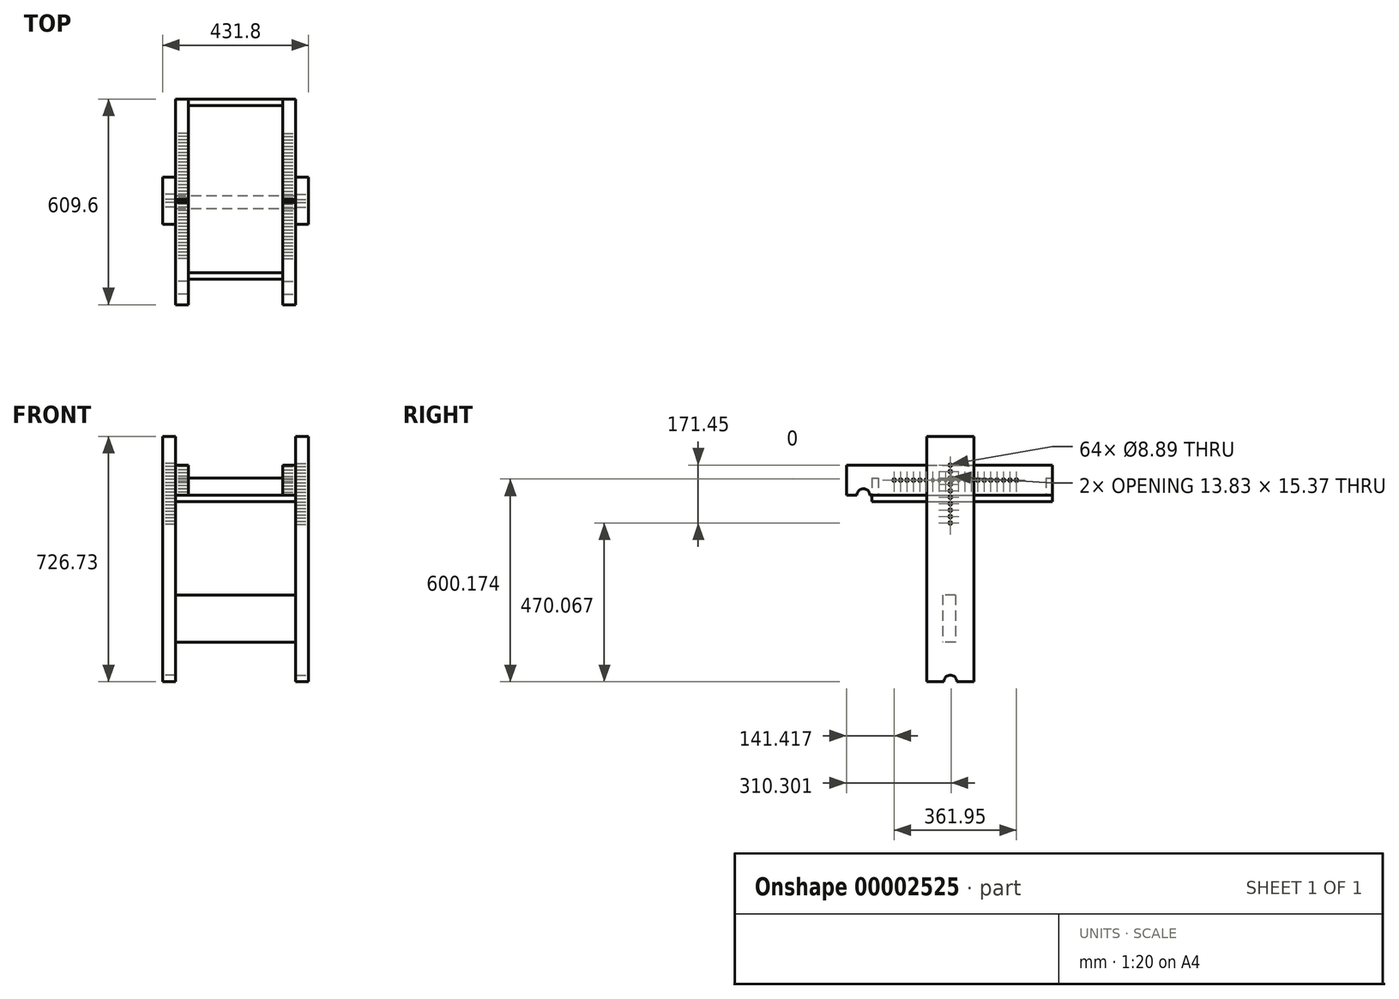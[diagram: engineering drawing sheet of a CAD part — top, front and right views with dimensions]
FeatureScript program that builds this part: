
annotation { "Feature Type Name" : "Feature", "Feature Type Description" : "" }
export const myFeature = defineFeature(function(context is Context, id is Id, definition is map)
    precondition{}
    {
        {
            var Q0;
            Q0=qCreatedBy(makeId("Right.planeOp"),FACE);
            var sketch = newSketch(context, id + "F0", { "sketchPlane" : qUnion([Q0])});
            skLineSegment(sketch, "E0", {"start": v(-273.03, 718.1) * mm, "end": v(285.89, -480.5) * mm, "construction": true});
            skLineSegment(sketch, "E1", {"start": v(-191.78, 754.22) * mm, "end": v(359.92, -428.91) * mm, "construction": true});
            skLineSegment(sketch, "E2", {"start": v(285.89, -480.5) * mm, "end": v(-310.41, -480.5) * mm, "construction": true});
            skLineSegment(sketch, "E3", {"start": v(-170.79, 498.85) * mm, "end": v(-90.22, 536.42) * mm, "construction": true});
            skCircle(sketch, "E4", {"center": v(-130.5, 517.63) * mm, "radius": 19.05 * mm, "construction": true});
            skLineSegment(sketch, "E5", {"start": v(86.84, -53.64) * mm, "end": v(167.41, -16.07) * mm, "construction": true});
            skCircle(sketch, "E6", {"center": v(127.13, -34.85) * mm, "radius": 19.05 * mm, "construction": true});
            skSolve(sketch);
        }
        {
            var Q0;
            Q0=qCreatedBy(makeId("Right.planeOp"),FACE);
            var sketch = newSketch(context, id + "F1", { "sketchPlane" : qUnion([Q0])});
            skLineSegment(sketch, "E7.bottom", {"start": v(-180.61, 606.53) * mm, "end": v(428.99, 606.53) * mm});
            skLineSegment(sketch, "E7.top", {"start": v(-180.61, 517.63) * mm, "end": v(428.99, 517.63) * mm});
            skLineSegment(sketch, "E7.left", {"start": v(-180.61, 606.53) * mm, "end": v(-180.61, 517.63) * mm});
            skLineSegment(sketch, "E7.right", {"start": v(428.99, 606.53) * mm, "end": v(428.99, 517.63) * mm});
            skSolve(sketch);
        }
        {
            var Q0;
            Q0 = qSketchRegion(id + "F1", true);
            extrude(context, id + "F2", {"entities" : qUnion([Q0]), "oppositeDirection" : true, "depth" : 38.1 * mm});
        }
        {
            var Q0;
            Q0=makeQuery(id+"F2.opExtrude","CAP_FACE",FACE,{"disambiguationData":[OSD([sQuery(id+"F1.wireOp",EDGE,"E7.bottom"),sQuery(id+"F1.wireOp",EDGE,"E7.top"),sQuery(id+"F1.wireOp",EDGE,"E7.left"),sQuery(id+"F1.wireOp",EDGE,"E7.right")])],"isStart":true});
            var sketch = newSketch(context, id + "F3", { "sketchPlane" : qUnion([Q0])});
            skLineSegment(sketch, "E8", {"start": v(-180.61, 562.08) * mm, "end": v(428.99, 562.08) * mm, "construction": true});
            skCircle(sketch, "E9", {"center": v(-39.2, 562.08) * mm, "radius": 4.45 * mm});
            skCircle(sketch, "E10.1.0.0", {"center": v(-20.14, 562.08) * mm, "radius": 4.45 * mm});
            skCircle(sketch, "E10.2.0.0", {"center": v(-1.1, 562.08) * mm, "radius": 4.45 * mm});
            skCircle(sketch, "E10.3.0.0", {"center": v(17.96, 562.08) * mm, "radius": 4.45 * mm});
            skCircle(sketch, "E10.4.0.0", {"center": v(37, 562.08) * mm, "radius": 4.45 * mm});
            skCircle(sketch, "E10.5.0.0", {"center": v(56.06, 562.08) * mm, "radius": 4.45 * mm});
            skCircle(sketch, "E10.6.0.0", {"center": v(75.1, 562.08) * mm, "radius": 4.45 * mm});
            skCircle(sketch, "E10.7.0.0", {"center": v(94.16, 562.08) * mm, "radius": 4.45 * mm});
            skCircle(sketch, "E10.8.0.0", {"center": v(113.2, 562.08) * mm, "radius": 4.45 * mm});
            skCircle(sketch, "E10.9.0.0", {"center": v(132.26, 562.08) * mm, "radius": 4.45 * mm});
            skCircle(sketch, "E10.10.0.0", {"center": v(151.3, 562.08) * mm, "radius": 4.45 * mm});
            skCircle(sketch, "E10.11.0.0", {"center": v(170.36, 562.08) * mm, "radius": 4.45 * mm});
            skCircle(sketch, "E10.12.0.0", {"center": v(189.4, 562.08) * mm, "radius": 4.45 * mm});
            skCircle(sketch, "E10.13.0.0", {"center": v(208.46, 562.08) * mm, "radius": 4.45 * mm});
            skCircle(sketch, "E10.14.0.0", {"center": v(227.5, 562.08) * mm, "radius": 4.45 * mm});
            skCircle(sketch, "E10.15.0.0", {"center": v(246.56, 562.08) * mm, "radius": 4.45 * mm});
            skCircle(sketch, "E10.16.0.0", {"center": v(265.6, 562.08) * mm, "radius": 4.45 * mm});
            skCircle(sketch, "E10.17.0.0", {"center": v(284.66, 562.08) * mm, "radius": 4.45 * mm});
            skCircle(sketch, "E10.18.0.0", {"center": v(303.7, 562.08) * mm, "radius": 4.45 * mm});
            skCircle(sketch, "E10.19.0.0", {"center": v(322.76, 562.08) * mm, "radius": 4.45 * mm});
            skLineSegment(sketch, "E10.direction1", {"start": v(-39.2, 562.08) * mm, "end": v(-20.14, 562.08) * mm, "construction": true});
            skSolve(sketch);
        }
        {
            var Q0;
            Q0 = qSketchRegion(id + "F3", true);
            extrude(context, id + "F4", {"entities" : qUnion([Q0]), "operationType" : NewBodyOperationType.REMOVE, "endBound" : BoundingType.THROUGH_ALL, "oppositeDirection" : true, "depth" : 25.4 * mm});
        }
        {
            var Q0;
            Q0=qCreatedBy(makeId("Right.planeOp"),FACE);
            var sketch = newSketch(context, id + "F5", { "sketchPlane" : qUnion([Q0])});
            skLineSegment(sketch, "E11.bottom", {"start": v(57.28, 691.88) * mm, "end": v(196.98, 691.88) * mm});
            skLineSegment(sketch, "E11.top", {"start": v(57.28, -34.85) * mm, "end": v(196.98, -34.85) * mm});
            skLineSegment(sketch, "E11.left", {"start": v(57.28, 691.88) * mm, "end": v(57.28, -34.85) * mm});
            skLineSegment(sketch, "E11.right", {"start": v(196.98, 691.88) * mm, "end": v(196.98, -34.85) * mm});
            skSolve(sketch);
        }
        {
            var Q0;
            Q0 = qSketchRegion(id + "F5", true);
            extrude(context, id + "F6", {"entities" : qUnion([Q0]), "depth" : 38.1 * mm});
        }
        {
            var Q0;
            Q0=makeQuery(id+"F6.opExtrude","CAP_FACE",FACE,{"disambiguationData":[OSD([sQuery(id+"F5.wireOp",EDGE,"E11.bottom"),sQuery(id+"F5.wireOp",EDGE,"E11.top"),sQuery(id+"F5.wireOp",EDGE,"E11.left"),sQuery(id+"F5.wireOp",EDGE,"E11.right")])],"isStart":false});
            var sketch = newSketch(context, id + "F7", { "sketchPlane" : qUnion([Q0])});
            skLineSegment(sketch, "E12", {"start": v(127.13, 691.88) * mm, "end": v(127.13, 283.48) * mm, "construction": true});
            skCircle(sketch, "E13", {"center": v(127.13, 606.67) * mm, "radius": 4.45 * mm});
            skCircle(sketch, "E14.0.1.0", {"center": v(127.13, 587.62) * mm, "radius": 4.45 * mm});
            skCircle(sketch, "E14.0.2.0", {"center": v(127.13, 568.57) * mm, "radius": 4.45 * mm});
            skCircle(sketch, "E14.0.3.0", {"center": v(127.13, 549.52) * mm, "radius": 4.45 * mm});
            skCircle(sketch, "E14.0.4.0", {"center": v(127.13, 530.47) * mm, "radius": 4.45 * mm});
            skCircle(sketch, "E14.0.5.0", {"center": v(127.13, 511.42) * mm, "radius": 4.45 * mm});
            skCircle(sketch, "E14.0.6.0", {"center": v(127.13, 492.37) * mm, "radius": 4.45 * mm});
            skCircle(sketch, "E14.0.7.0", {"center": v(127.13, 473.32) * mm, "radius": 4.45 * mm});
            skCircle(sketch, "E14.0.8.0", {"center": v(127.13, 454.27) * mm, "radius": 4.45 * mm});
            skCircle(sketch, "E14.0.9.0", {"center": v(127.13, 435.22) * mm, "radius": 4.45 * mm});
            skLineSegment(sketch, "E14.direction1", {"start": v(127.13, 606.67) * mm, "end": v(149.47, 606.1) * mm, "construction": true});
            skLineSegment(sketch, "E14.direction2", {"start": v(127.13, 606.67) * mm, "end": v(127.13, 587.62) * mm, "construction": true});
            skSolve(sketch);
        }
        {
            var Q0;
            Q0 = qSketchRegion(id + "F7", true);
            extrude(context, id + "F8", {"entities" : qUnion([Q0]), "operationType" : NewBodyOperationType.REMOVE, "endBound" : BoundingType.THROUGH_ALL, "oppositeDirection" : true, "depth" : 25.4 * mm});
        }
        {
            var Q0;
            {var subQ0=sQuery(id+"F1.wireOp",EDGE,"E7.left");var subQ1=sQuery(id+"F1.wireOp",EDGE,"E7.top");var subQ3=sQuery(id+"F1.wireOp",EDGE,"E7.bottom");Q0=makeQuery(id+"F6.boolean.opBoolean","SPLIT",FACE,{"disambiguationData":[TD([makeQuery(id+"F2.opExtrude","SWEPT_FACE",FACE,{"disambiguationData":[OSD([subQ0])]})])],"derivedFrom":makeQuery(id+"F2.opExtrude","CAP_FACE",FACE,{"disambiguationData":[OSD([subQ3,subQ1,subQ0,sQuery(id+"F1.wireOp",EDGE,"E7.right")])],"isStart":true})});}
            var sketch = newSketch(context, id + "F9", { "sketchPlane" : qUnion([Q0])});
            skCircle(sketch, "E15.0", {"center": v(-130.5, 517.63) * mm, "radius": 19.05 * mm});
            skSolve(sketch);
        }
        {
            var Q0;
            Q0 = qSketchRegion(id + "F9", true);
            extrude(context, id + "F10", {"entities" : qUnion([Q0]), "operationType" : NewBodyOperationType.REMOVE, "endBound" : BoundingType.THROUGH_ALL, "oppositeDirection" : true, "depth" : 25.4 * mm});
        }
        {
            var Q0;
            Q0=makeQuery(id+"F6.opExtrude","CAP_FACE",FACE,{"disambiguationData":[OSD([sQuery(id+"F5.wireOp",EDGE,"E11.bottom"),sQuery(id+"F5.wireOp",EDGE,"E11.top"),sQuery(id+"F5.wireOp",EDGE,"E11.left"),sQuery(id+"F5.wireOp",EDGE,"E11.right")])],"isStart":false});
            var sketch = newSketch(context, id + "F11", { "sketchPlane" : qUnion([Q0])});
            skCircle(sketch, "E16.0", {"center": v(127.13, -34.85) * mm, "radius": 19.05 * mm});
            skSolve(sketch);
        }
        {
            var Q0;
            Q0 = qSketchRegion(id + "F11", true);
            extrude(context, id + "F12", {"entities" : qUnion([Q0]), "operationType" : NewBodyOperationType.REMOVE, "endBound" : BoundingType.THROUGH_ALL, "oppositeDirection" : true, "depth" : 25.4 * mm});
        }
        {
            var Q0;
            Q0=makeQuery(id+"F2.opExtrude","CAP_FACE",FACE,{"disambiguationData":[OSD([sQuery(id+"F1.wireOp",EDGE,"E7.bottom"),sQuery(id+"F1.wireOp",EDGE,"E7.top"),sQuery(id+"F1.wireOp",EDGE,"E7.left"),sQuery(id+"F1.wireOp",EDGE,"E7.right")])],"isStart":true});
            var sketch = newSketch(context, id + "F13", { "sketchPlane" : qUnion([Q0])});
            skLineSegment(sketch, "E17.bottom", {"start": v(-105.1, 517.63) * mm, "end": v(428.99, 517.63) * mm});
            skLineSegment(sketch, "E17.top", {"start": v(-105.1, 498.58) * mm, "end": v(428.99, 498.58) * mm});
            skLineSegment(sketch, "E17.left", {"start": v(-105.1, 517.63) * mm, "end": v(-105.1, 498.58) * mm});
            skLineSegment(sketch, "E17.right", {"start": v(428.99, 517.63) * mm, "end": v(428.99, 498.58) * mm});
            skSolve(sketch);
        }
        {
            var Q0;
            Q0 = qSketchRegion(id + "F13", true);
            extrude(context, id + "F14", {"entities" : qUnion([Q0]), "oppositeDirection" : true, "depth" : 355.6 * mm});
        }
        {
            var Q0;
            Q0=makeQuery(id+"F14.opExtrude","CAP_FACE",FACE,{"disambiguationData":[OSD([sQuery(id+"F13.wireOp",EDGE,"E17.bottom"),sQuery(id+"F13.wireOp",EDGE,"E17.top"),sQuery(id+"F13.wireOp",EDGE,"E17.left"),sQuery(id+"F13.wireOp",EDGE,"E17.right")])],"isStart":true});
            var Q1;
            Q1=makeQuery(id+"F14.opExtrude","CAP_FACE",FACE,{"disambiguationData":[OSD([sQuery(id+"F13.wireOp",EDGE,"E17.bottom"),sQuery(id+"F13.wireOp",EDGE,"E17.top"),sQuery(id+"F13.wireOp",EDGE,"E17.left"),sQuery(id+"F13.wireOp",EDGE,"E17.right")])],"isStart":false});
            cPlane(context, id + "F15", {"entities" : qUnion([Q0, Q1]), "cplaneType" : CPlaneType.MID_PLANE, "offset" : 25.4 * mm, "width" : 152.4 * mm, "height" : 152.4 * mm});
        }
        {
            var Q0;
            Q0=makeQuery(id+"F2.opExtrude","SWEPT_BODY",BODY,{"disambiguationData":[OSD([sQuery(id+"F1.wireOp",EDGE,"E7.bottom"),sQuery(id+"F1.wireOp",EDGE,"E7.top"),sQuery(id+"F1.wireOp",EDGE,"E7.left"),sQuery(id+"F1.wireOp",EDGE,"E7.right")])]});
            var Q1;
            Q1=makeQuery(id+"F6.opExtrude","SWEPT_BODY",BODY,{"disambiguationData":[OSD([sQuery(id+"F5.wireOp",EDGE,"E11.bottom"),sQuery(id+"F5.wireOp",EDGE,"E11.top"),sQuery(id+"F5.wireOp",EDGE,"E11.left"),sQuery(id+"F5.wireOp",EDGE,"E11.right")])]});
            var Q2;
            Q2=qCreatedBy(id+"F15.planeOp",FACE);
            mirror(context, id + "F16", {"entities" : qUnion([Q0, Q1]), "mirrorPlane" : qUnion([Q2])});
        }
        {
            var Q0;
            Q0=makeQuery(id+"F6.opExtrude","CAP_FACE",FACE,{"disambiguationData":[OSD([sQuery(id+"F5.wireOp",EDGE,"E11.bottom"),sQuery(id+"F5.wireOp",EDGE,"E11.top"),sQuery(id+"F5.wireOp",EDGE,"E11.left"),sQuery(id+"F5.wireOp",EDGE,"E11.right")])],"isStart":true});
            var sketch = newSketch(context, id + "F17", { "sketchPlane" : qUnion([Q0])});
            skLineSegment(sketch, "E18.bottom", {"start": v(-142.4, 221.73) * mm, "end": v(-104.3, 221.73) * mm});
            skLineSegment(sketch, "E18.top", {"start": v(-142.4, 82.03) * mm, "end": v(-104.3, 82.03) * mm});
            skLineSegment(sketch, "E18.left", {"start": v(-142.4, 221.73) * mm, "end": v(-142.4, 82.03) * mm});
            skLineSegment(sketch, "E18.right", {"start": v(-104.3, 221.73) * mm, "end": v(-104.3, 82.03) * mm});
            skSolve(sketch);
        }
        {
            var Q0;
            Q0 = qSketchRegion(id + "F17", true);
            var Q1;
            Q1=makeQuery(id+"F16.opPattern","COPY",FACE,{"derivedFrom":makeQuery(id+"F6.opExtrude","CAP_FACE",FACE,{"disambiguationData":[OSD([sQuery(id+"F5.wireOp",EDGE,"E11.bottom"),sQuery(id+"F5.wireOp",EDGE,"E11.top"),sQuery(id+"F5.wireOp",EDGE,"E11.left"),sQuery(id+"F5.wireOp",EDGE,"E11.right")])],"isStart":true}),"instanceName":"1"});
            extrude(context, id + "F18", {"entities" : qUnion([Q0]), "endBound" : BoundingType.UP_TO_SURFACE, "endBoundEntityFace" : qUnion([Q1]), "depth" : 25.4 * mm});
        }
        {
            var Q0;
            Q0=makeQuery(id+"F14.opExtrude","SWEPT_FACE",FACE,{"disambiguationData":[OSD([sQuery(id+"F13.wireOp",EDGE,"E17.bottom")])]});
            var sketch = newSketch(context, id + "F19", { "sketchPlane" : qUnion([Q0])});
            skLineSegment(sketch, "E19.bottom", {"start": v(-317.5, -105.1) * mm, "end": v(-38.1, -105.1) * mm});
            skLineSegment(sketch, "E19.top", {"start": v(-317.5, -86.05) * mm, "end": v(-38.1, -86.05) * mm});
            skLineSegment(sketch, "E19.left", {"start": v(-317.5, -105.1) * mm, "end": v(-317.5, -86.05) * mm});
            skLineSegment(sketch, "E19.right", {"start": v(-38.1, -105.1) * mm, "end": v(-38.1, -86.05) * mm});
            skLineSegment(sketch, "E20.bottom", {"start": v(-317.5, 409.94) * mm, "end": v(-38.1, 409.94) * mm});
            skLineSegment(sketch, "E20.top", {"start": v(-317.5, 428.99) * mm, "end": v(-38.1, 428.99) * mm});
            skLineSegment(sketch, "E20.left", {"start": v(-317.5, 409.94) * mm, "end": v(-317.5, 428.99) * mm});
            skLineSegment(sketch, "E20.right", {"start": v(-38.1, 409.94) * mm, "end": v(-38.1, 428.99) * mm});
            skSolve(sketch);
        }
        {
            var Q0;
            Q0 = qSketchRegion(id + "F19", true);
            extrude(context, id + "F20", {"entities" : qUnion([Q0]), "depth" : 50.8 * mm});
        }
    });
